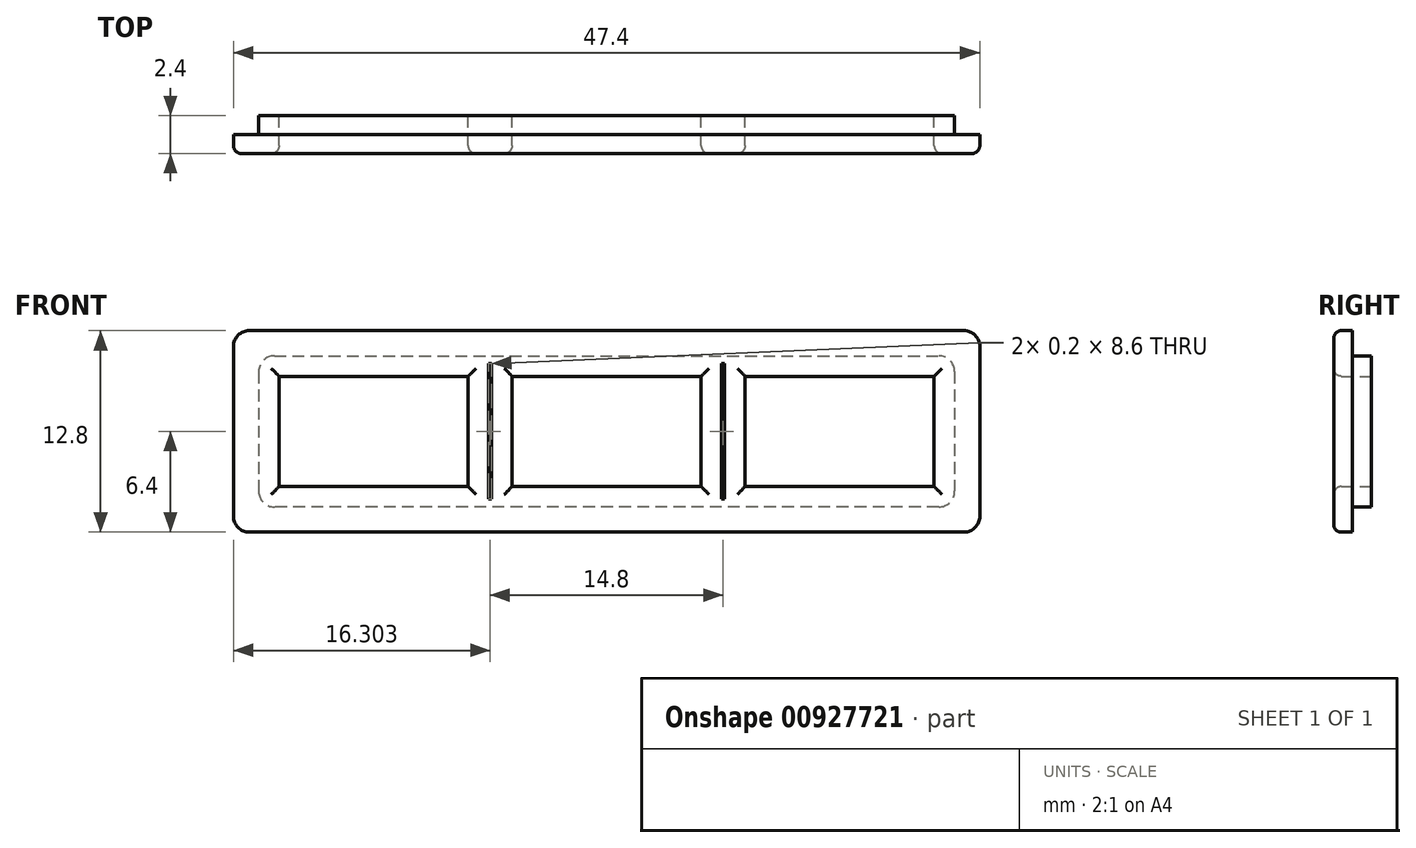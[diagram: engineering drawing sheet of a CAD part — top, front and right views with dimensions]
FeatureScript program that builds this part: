
annotation { "Feature Type Name" : "Feature", "Feature Type Description" : "" }
export const myFeature = defineFeature(function(context is Context, id is Id, definition is map)
    precondition{}
    {
        {
            var Q0;
            Q0=qCreatedBy(makeId("Front.planeOp"),FACE);
            var sketch = newSketch(context, id + "F0", { "sketchPlane" : qUnion([Q0])});
            skLineSegment(sketch, "E0.bottom", {"start": v(66.88, 6.3) * mm, "end": v(78.88, 6.3) * mm});
            skLineSegment(sketch, "E0.top", {"start": v(66.88, -0.7) * mm, "end": v(78.88, -0.7) * mm});
            skLineSegment(sketch, "E0.left", {"start": v(66.88, 6.3) * mm, "end": v(66.88, -0.7) * mm});
            skLineSegment(sketch, "E0.right", {"start": v(78.88, 6.3) * mm, "end": v(78.88, -0.7) * mm});
            skPoint(sketch, "E0.middle", {"position": v(72.88, 2.8) * mm});
            skLineSegment(sketch, "E1.right", {"start": v(80.18, 7.6) * mm, "end": v(80.18, -2) * mm});
            skLineSegment(sketch, "E2", {"start": v(65.58, -1.5) * mm, "end": v(65.38, -1.5) * mm});
            skLineSegment(sketch, "E3", {"start": v(65.58, 7.1) * mm, "end": v(65.38, 7.1) * mm});
            skPoint(sketch, "E4.1.0.2", {"position": v(58.08, 2.8) * mm});
            skLineSegment(sketch, "E4.1.0.3", {"start": v(52.08, 6.3) * mm, "end": v(52.08, -0.7) * mm});
            skLineSegment(sketch, "E4.1.0.4", {"start": v(64.08, 6.3) * mm, "end": v(64.08, -0.7) * mm});
            skLineSegment(sketch, "E4.1.0.5", {"start": v(52.08, 6.3) * mm, "end": v(64.08, 6.3) * mm});
            skLineSegment(sketch, "E4.1.0.8", {"start": v(52.08, -0.7) * mm, "end": v(64.08, -0.7) * mm});
            skPoint(sketch, "E4.1.0.9", {"position": v(58.08, 2.8) * mm});
            skLineSegment(sketch, "E4.1.0.12", {"start": v(50.78, 7.1) * mm, "end": v(50.58, 7.1) * mm});
            skLineSegment(sketch, "E4.1.0.16", {"start": v(50.78, -1.5) * mm, "end": v(50.58, -1.5) * mm});
            skPoint(sketch, "E4.2.0.2", {"position": v(43.28, 2.8) * mm});
            skLineSegment(sketch, "E4.2.0.3", {"start": v(37.28, 6.3) * mm, "end": v(37.28, -0.7) * mm});
            skLineSegment(sketch, "E4.2.0.4", {"start": v(49.28, 6.3) * mm, "end": v(49.28, -0.7) * mm});
            skLineSegment(sketch, "E4.2.0.5", {"start": v(37.28, 6.3) * mm, "end": v(49.28, 6.3) * mm});
            skLineSegment(sketch, "E4.2.0.8", {"start": v(37.28, -0.7) * mm, "end": v(49.28, -0.7) * mm});
            skPoint(sketch, "E4.2.0.9", {"position": v(43.28, 2.8) * mm});
            skLineSegment(sketch, "E5", {"start": v(35.98, 7.6) * mm, "end": v(35.98, -2) * mm});
            skLineSegment(sketch, "E6", {"start": v(65.58, 7.1) * mm, "end": v(65.58, -1.5) * mm});
            skLineSegment(sketch, "E7", {"start": v(65.38, 7.1) * mm, "end": v(65.38, -1.5) * mm});
            skLineSegment(sketch, "E8", {"start": v(50.58, 7.1) * mm, "end": v(50.58, -1.5) * mm});
            skLineSegment(sketch, "E9", {"start": v(50.78, -1.5) * mm, "end": v(50.78, 7.1) * mm});
            skLineSegment(sketch, "E10", {"start": v(35.98, 7.6) * mm, "end": v(80.18, 7.6) * mm});
            skLineSegment(sketch, "E11", {"start": v(80.18, -2) * mm, "end": v(35.98, -2) * mm});
            skSolve(sketch);
        }
        {
            var Q0;
            Q0=makeQuery(id+"F0.imprint","IMPRINT",FACE,{"disambiguationData":[TD([[makeQuery(id+"F0.imprint","IMPRINT",EDGE,{"derivedFrom":sQuery(id+"F0.wireOp",EDGE,"E4.2.0.0")}),1.0]])]});
            var Q1;
            Q1=makeQuery(id+"F0.imprint","IMPRINT",FACE,{"disambiguationData":[TD([[makeQuery(id+"F0.imprint","IMPRINT",EDGE,{"derivedFrom":sQuery(id+"F0.wireOp",EDGE,"E4.1.0.0")}),1.0]])]});
            var Q2;
            Q2=makeQuery(id+"F0.imprint","IMPRINT",FACE,{"disambiguationData":[TD([[makeQuery(id+"F0.imprint","IMPRINT",EDGE,{"derivedFrom":sQuery(id+"F0.wireOp",EDGE,"E0.bottom")}),1.0]])]});
            var Q3;
            {var subQ2=sQuery(id+"F0.wireOp",EDGE,"E4.2.0.1");Q3=makeQuery(id+"F0.imprint","IMPRINT",FACE,{"disambiguationData":[TD([[makeQuery(id+"F0.imprint","IMPRINT",EDGE,{"derivedFrom":subQ2}),1.0]])]});}
            extrude(context, id + "F1", {"entities" : qUnion([Q0, Q1, Q2, Q3]), "depth" : 2.4 * mm, "offsetDistance" : 25 * mm});
        }
        {
            var Q0;
            Q0=makeQuery(id+"F1.opExtrude","CAP_EDGE",EDGE,{"disambiguationData":[OSD([sQuery(id+"F0.wireOp",EDGE,"E4.2.0.5")])],"isStart":false});
            var Q1;
            Q1=makeQuery(id+"F1.opExtrude","CAP_EDGE",EDGE,{"disambiguationData":[OSD([sQuery(id+"F0.wireOp",EDGE,"E4.2.0.3")])],"isStart":false});
            var Q2;
            Q2=makeQuery(id+"F1.opExtrude","CAP_EDGE",EDGE,{"disambiguationData":[OSD([sQuery(id+"F0.wireOp",EDGE,"E4.2.0.4")])],"isStart":false});
            var Q3;
            Q3=makeQuery(id+"F1.opExtrude","CAP_EDGE",EDGE,{"disambiguationData":[OSD([sQuery(id+"F0.wireOp",EDGE,"E4.1.0.5")])],"isStart":false});
            var Q4;
            Q4=makeQuery(id+"F1.opExtrude","CAP_EDGE",EDGE,{"disambiguationData":[OSD([sQuery(id+"F0.wireOp",EDGE,"E4.1.0.3")])],"isStart":false});
            var Q5;
            Q5=makeQuery(id+"F1.opExtrude","CAP_EDGE",EDGE,{"disambiguationData":[OSD([sQuery(id+"F0.wireOp",EDGE,"E4.1.0.8")])],"isStart":false});
            var Q6;
            Q6=makeQuery(id+"F1.opExtrude","CAP_EDGE",EDGE,{"disambiguationData":[OSD([sQuery(id+"F0.wireOp",EDGE,"E4.2.0.8")])],"isStart":false});
            var Q7;
            Q7=makeQuery(id+"F1.opExtrude","CAP_EDGE",EDGE,{"disambiguationData":[OSD([sQuery(id+"F0.wireOp",EDGE,"E4.1.0.4")])],"isStart":false});
            var Q8;
            Q8=makeQuery(id+"F1.opExtrude","CAP_EDGE",EDGE,{"disambiguationData":[OSD([sQuery(id+"F0.wireOp",EDGE,"E0.left")])],"isStart":false});
            var Q9;
            Q9=makeQuery(id+"F1.opExtrude","CAP_EDGE",EDGE,{"disambiguationData":[OSD([sQuery(id+"F0.wireOp",EDGE,"E0.top")])],"isStart":false});
            var Q10;
            Q10=makeQuery(id+"F1.opExtrude","CAP_EDGE",EDGE,{"disambiguationData":[OSD([sQuery(id+"F0.wireOp",EDGE,"E0.bottom")])],"isStart":false});
            var Q11;
            Q11=makeQuery(id+"F1.opExtrude","CAP_EDGE",EDGE,{"disambiguationData":[OSD([sQuery(id+"F0.wireOp",EDGE,"E0.right")])],"isStart":false});
            fillet(context, id + "F2", {"entities" : qUnion([Q0, Q1, Q2, Q3, Q4, Q5, Q6, Q7, Q8, Q9, Q10, Q11]), "radius" : .5 * mm, "tangentPropagation" : true, "allowEdgeOverflow" : false});
        }
        {
            var Q0;
            Q0=makeQuery(id+"F1.opExtrude","SWEPT_FACE",FACE,{"disambiguationData":[OSD([sQuery(id+"F0.wireOp",EDGE,"E11")])]});
            var sketch = newSketch(context, id + "F3", { "sketchPlane" : qUnion([Q0])});
            skLineSegment(sketch, "E12.bottom", {"start": v(35.98, 2.4) * mm, "end": v(80.18, 2.4) * mm});
            skLineSegment(sketch, "E12.top", {"start": v(35.98, 1.2) * mm, "end": v(80.18, 1.2) * mm});
            skLineSegment(sketch, "E12.left", {"start": v(35.98, 2.4) * mm, "end": v(35.98, 1.2) * mm});
            skLineSegment(sketch, "E12.right", {"start": v(80.18, 2.4) * mm, "end": v(80.18, 1.2) * mm});
            skSolve(sketch);
        }
        {
            var Q0;
            Q0=makeQuery(id+"F3.imprint","IMPRINT",FACE,{"disambiguationData":[TD([[makeQuery(id+"F3.imprint","IMPRINT",EDGE,{"derivedFrom":sQuery(id+"F3.wireOp",EDGE,"E12.bottom")}),1.0]])]});
            extrude(context, id + "F4", {"entities" : qUnion([Q0]), "operationType" : NewBodyOperationType.ADD, "depth" : 1.6 * mm, "offsetDistance" : 25 * mm});
        }
        {
            var Q0;
            Q0=makeQuery(id+"F1.opExtrude","SWEPT_FACE",FACE,{"disambiguationData":[OSD([sQuery(id+"F0.wireOp",EDGE,"E10")])]});
            var sketch = newSketch(context, id + "F5", { "sketchPlane" : qUnion([Q0])});
            skLineSegment(sketch, "E13.bottom", {"start": v(35.98, -2.4) * mm, "end": v(80.18, -2.4) * mm});
            skLineSegment(sketch, "E13.top", {"start": v(35.98, -1.2) * mm, "end": v(80.18, -1.2) * mm});
            skLineSegment(sketch, "E13.left", {"start": v(35.98, -2.4) * mm, "end": v(35.98, -1.2) * mm});
            skLineSegment(sketch, "E13.right", {"start": v(80.18, -2.4) * mm, "end": v(80.18, -1.2) * mm});
            skSolve(sketch);
        }
        {
            var Q0;
            Q0=makeQuery(id+"F5.imprint","IMPRINT",FACE,{"disambiguationData":[TD([[makeQuery(id+"F5.imprint","IMPRINT",EDGE,{"derivedFrom":sQuery(id+"F5.wireOp",EDGE,"E13.bottom")}),1.0]])]});
            extrude(context, id + "F6", {"entities" : qUnion([Q0]), "operationType" : NewBodyOperationType.ADD, "depth" : 1.6 * mm, "offsetDistance" : 25 * mm});
        }
        {
            var Q0;
            Q0=makeQuery(id+"F6.boolean.opBoolean","MERGE",FACE,{"derivedFrom":[makeQuery(id+"F4.boolean.opBoolean","MERGE",FACE,{"derivedFrom":[makeQuery(id+"F1.opExtrude","SWEPT_FACE",FACE,{"disambiguationData":[OSD([sQuery(id+"F0.wireOp",EDGE,"E5")])]}),makeQuery(id+"F4.opExtrude","SWEPT_FACE",FACE,{"disambiguationData":[OSD([sQuery(id+"F3.wireOp",EDGE,"E12.left")])]})]}),makeQuery(id+"F6.opExtrude","SWEPT_FACE",FACE,{"disambiguationData":[OSD([sQuery(id+"F5.wireOp",EDGE,"E13.left")])]})]});
            var sketch = newSketch(context, id + "F7", { "sketchPlane" : qUnion([Q0])});
            skLineSegment(sketch, "E14.bottom", {"start": v(2.4, 9.2) * mm, "end": v(1.2, 9.2) * mm});
            skLineSegment(sketch, "E14.top", {"start": v(2.4, -3.6) * mm, "end": v(1.2, -3.6) * mm});
            skLineSegment(sketch, "E14.left", {"start": v(2.4, 9.2) * mm, "end": v(2.4, -3.6) * mm});
            skLineSegment(sketch, "E14.right", {"start": v(1.2, 9.2) * mm, "end": v(1.2, -3.6) * mm});
            skSolve(sketch);
        }
        {
            var Q0;
            {var subQ5=sQuery(id+"F7.wireOp",EDGE,"E14.bottom");Q0=makeQuery(id+"F7.imprint","IMPRINT",FACE,{"disambiguationData":[TD([[makeQuery(id+"F7.imprint","IMPRINT",EDGE,{"derivedFrom":subQ5}),1.0]])]});}
            extrude(context, id + "F8", {"entities" : qUnion([Q0]), "operationType" : NewBodyOperationType.ADD, "depth" : 1.6 * mm, "offsetDistance" : 25 * mm});
        }
        {
            var Q0;
            Q0=makeQuery(id+"F6.boolean.opBoolean","MERGE",FACE,{"derivedFrom":[makeQuery(id+"F4.boolean.opBoolean","MERGE",FACE,{"derivedFrom":[makeQuery(id+"F1.opExtrude","SWEPT_FACE",FACE,{"disambiguationData":[OSD([sQuery(id+"F0.wireOp",EDGE,"E1.right")])]}),makeQuery(id+"F4.opExtrude","SWEPT_FACE",FACE,{"disambiguationData":[OSD([sQuery(id+"F3.wireOp",EDGE,"E12.right")])]})]}),makeQuery(id+"F6.opExtrude","SWEPT_FACE",FACE,{"disambiguationData":[OSD([sQuery(id+"F5.wireOp",EDGE,"E13.right")])]})]});
            var sketch = newSketch(context, id + "F9", { "sketchPlane" : qUnion([Q0])});
            skLineSegment(sketch, "E15.bottom", {"start": v(-2.4, 9.2) * mm, "end": v(-1.2, 9.2) * mm});
            skLineSegment(sketch, "E15.top", {"start": v(-2.4, -3.6) * mm, "end": v(-1.2, -3.6) * mm});
            skLineSegment(sketch, "E15.left", {"start": v(-2.4, 9.2) * mm, "end": v(-2.4, -3.6) * mm});
            skLineSegment(sketch, "E15.right", {"start": v(-1.2, 9.2) * mm, "end": v(-1.2, -3.6) * mm});
            skSolve(sketch);
        }
        {
            var Q0;
            {var subQ5=sQuery(id+"F9.wireOp",EDGE,"E15.bottom");Q0=makeQuery(id+"F9.imprint","IMPRINT",FACE,{"disambiguationData":[TD([[makeQuery(id+"F9.imprint","IMPRINT",EDGE,{"derivedFrom":subQ5}),-1.0]])]});}
            extrude(context, id + "F10", {"entities" : qUnion([Q0]), "operationType" : NewBodyOperationType.ADD, "depth" : 1.6 * mm, "offsetDistance" : 25 * mm});
        }
        {
            var Q0;
            Q0=makeQuery(id+"F10.boolean.opBoolean","MERGE",EDGE,{"derivedFrom":[makeQuery(id+"F8.boolean.opBoolean","MERGE",EDGE,{"derivedFrom":[makeQuery(id+"F6.opExtrude","CAP_EDGE",EDGE,{"disambiguationData":[OSD([sQuery(id+"F5.wireOp",EDGE,"E13.bottom")])],"isStart":false}),makeQuery(id+"F8.opExtrude","SWEPT_EDGE",EDGE,{"disambiguationData":[OSD([sQuery(id+"F7.wireOp",EDGE,"E14.bottom"),sQuery(id+"F7.wireOp",EDGE,"E14.left")])]})]}),makeQuery(id+"F10.opExtrude","SWEPT_EDGE",EDGE,{"disambiguationData":[OSD([sQuery(id+"F9.wireOp",EDGE,"E15.bottom"),sQuery(id+"F9.wireOp",EDGE,"E15.left")])]})]});
            var Q1;
            Q1=makeQuery(id+"F10.opExtrude","CAP_EDGE",EDGE,{"disambiguationData":[OSD([sQuery(id+"F9.wireOp",EDGE,"E15.left")])],"isStart":false});
            var Q2;
            Q2=makeQuery(id+"F10.boolean.opBoolean","MERGE",EDGE,{"derivedFrom":[makeQuery(id+"F8.boolean.opBoolean","MERGE",EDGE,{"derivedFrom":[makeQuery(id+"F4.opExtrude","CAP_EDGE",EDGE,{"disambiguationData":[OSD([sQuery(id+"F3.wireOp",EDGE,"E12.bottom")])],"isStart":false}),makeQuery(id+"F8.opExtrude","SWEPT_EDGE",EDGE,{"disambiguationData":[OSD([sQuery(id+"F7.wireOp",EDGE,"E14.top"),sQuery(id+"F7.wireOp",EDGE,"E14.left")])]})]}),makeQuery(id+"F10.opExtrude","SWEPT_EDGE",EDGE,{"disambiguationData":[OSD([sQuery(id+"F9.wireOp",EDGE,"E15.top"),sQuery(id+"F9.wireOp",EDGE,"E15.left")])]})]});
            var Q3;
            Q3=makeQuery(id+"F8.opExtrude","CAP_EDGE",EDGE,{"disambiguationData":[OSD([sQuery(id+"F7.wireOp",EDGE,"E14.left")])],"isStart":false});
            fillet(context, id + "F11", {"entities" : qUnion([Q0, Q1, Q2, Q3]), "radius" : .5 * mm, "tangentPropagation" : true, "allowEdgeOverflow" : false});
        }
        {
            var Q0;
            Q0=makeQuery(id+"F1.opExtrude","SWEPT_EDGE",EDGE,{"disambiguationData":[OSD([sQuery(id+"F0.wireOp",EDGE,"E5"),sQuery(id+"F0.wireOp",EDGE,"E10")])]});
            var Q1;
            Q1=makeQuery(id+"F1.opExtrude","SWEPT_EDGE",EDGE,{"disambiguationData":[OSD([sQuery(id+"F0.wireOp",EDGE,"E5"),sQuery(id+"F0.wireOp",EDGE,"E11")])]});
            var Q2;
            Q2=makeQuery(id+"F1.opExtrude","SWEPT_EDGE",EDGE,{"disambiguationData":[OSD([sQuery(id+"F0.wireOp",EDGE,"E1.right"),sQuery(id+"F0.wireOp",EDGE,"E11")])]});
            var Q3;
            Q3=makeQuery(id+"F1.opExtrude","SWEPT_EDGE",EDGE,{"disambiguationData":[OSD([sQuery(id+"F0.wireOp",EDGE,"E1.right"),sQuery(id+"F0.wireOp",EDGE,"E10")])]});
            var Q4;
            Q4=makeQuery(id+"F10.opExtrude","CAP_EDGE",EDGE,{"disambiguationData":[OSD([sQuery(id+"F9.wireOp",EDGE,"E15.bottom")])],"isStart":false});
            var Q5;
            Q5=makeQuery(id+"F10.opExtrude","CAP_EDGE",EDGE,{"disambiguationData":[OSD([sQuery(id+"F9.wireOp",EDGE,"E15.top")])],"isStart":false});
            var Q6;
            Q6=makeQuery(id+"F8.opExtrude","CAP_EDGE",EDGE,{"disambiguationData":[OSD([sQuery(id+"F7.wireOp",EDGE,"E14.top")])],"isStart":false});
            var Q7;
            Q7=makeQuery(id+"F8.opExtrude","CAP_EDGE",EDGE,{"disambiguationData":[OSD([sQuery(id+"F7.wireOp",EDGE,"E14.bottom")])],"isStart":false});
            fillet(context, id + "F12", {"entities" : qUnion([Q0, Q1, Q2, Q3, Q4, Q5, Q6, Q7]), "radius" : 1 * mm, "tangentPropagation" : true, "allowEdgeOverflow" : false});
        }
    });
